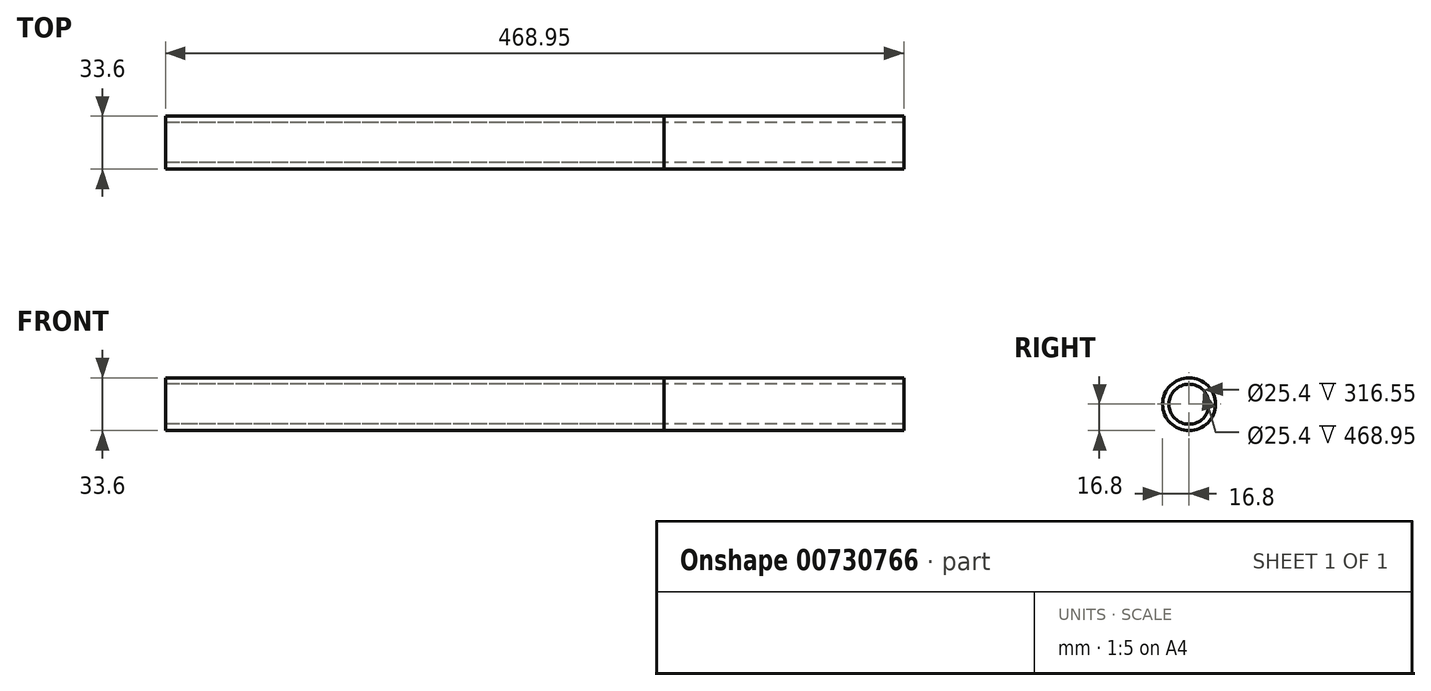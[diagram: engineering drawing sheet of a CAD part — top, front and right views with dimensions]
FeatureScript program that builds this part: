
annotation { "Feature Type Name" : "Feature", "Feature Type Description" : "" }
export const myFeature = defineFeature(function(context is Context, id is Id, definition is map)
    precondition{}
    {
        {
            var Q0;
            Q0=qCreatedBy(makeId("Right.planeOp"),FACE);
            var sketch = newSketch(context, id + "F0", { "sketchPlane" : qUnion([Q0])});
            skCircle(sketch, "E0", {"center": v(0, 0) * mm, "radius": 16.8 * mm});
            skCircle(sketch, "E1.0", {"center": v(0, 0) * mm, "radius": 12.7 * mm});
            skSolve(sketch);
        }
        {
            var Q0;
            Q0=makeQuery(id+"F0.imprint","IMPRINT",FACE,{"disambiguationData":[TD([[makeQuery(id+"F0.imprint","IMPRINT",EDGE,{"derivedFrom":sQuery(id+"F0.wireOp",EDGE,"E0")}),1.0]])]});
            extrude(context, id + "F1", {"entities" : qUnion([Q0]), "depth" : 488.95 * mm, "offsetDistance" : 25.4 * mm, "hasSecondDirection" : true, "secondDirectionOppositeDirection" : false, "secondDirectionDepth" : 20 * mm});
        }
        {
            var Q0;
            Q0=makeQuery(id+"F0.imprint","IMPRINT",FACE,{"disambiguationData":[TD([[makeQuery(id+"F0.imprint","IMPRINT",EDGE,{"derivedFrom":sQuery(id+"F0.wireOp",EDGE,"E0")}),1.0]])]});
            extrude(context, id + "F2", {"entities" : qUnion([Q0]), "depth" : 336.55 * mm, "offsetDistance" : 25 * mm, "hasSecondDirection" : true, "secondDirectionOppositeDirection" : false, "secondDirectionDepth" : 20 * mm});
        }
    });
